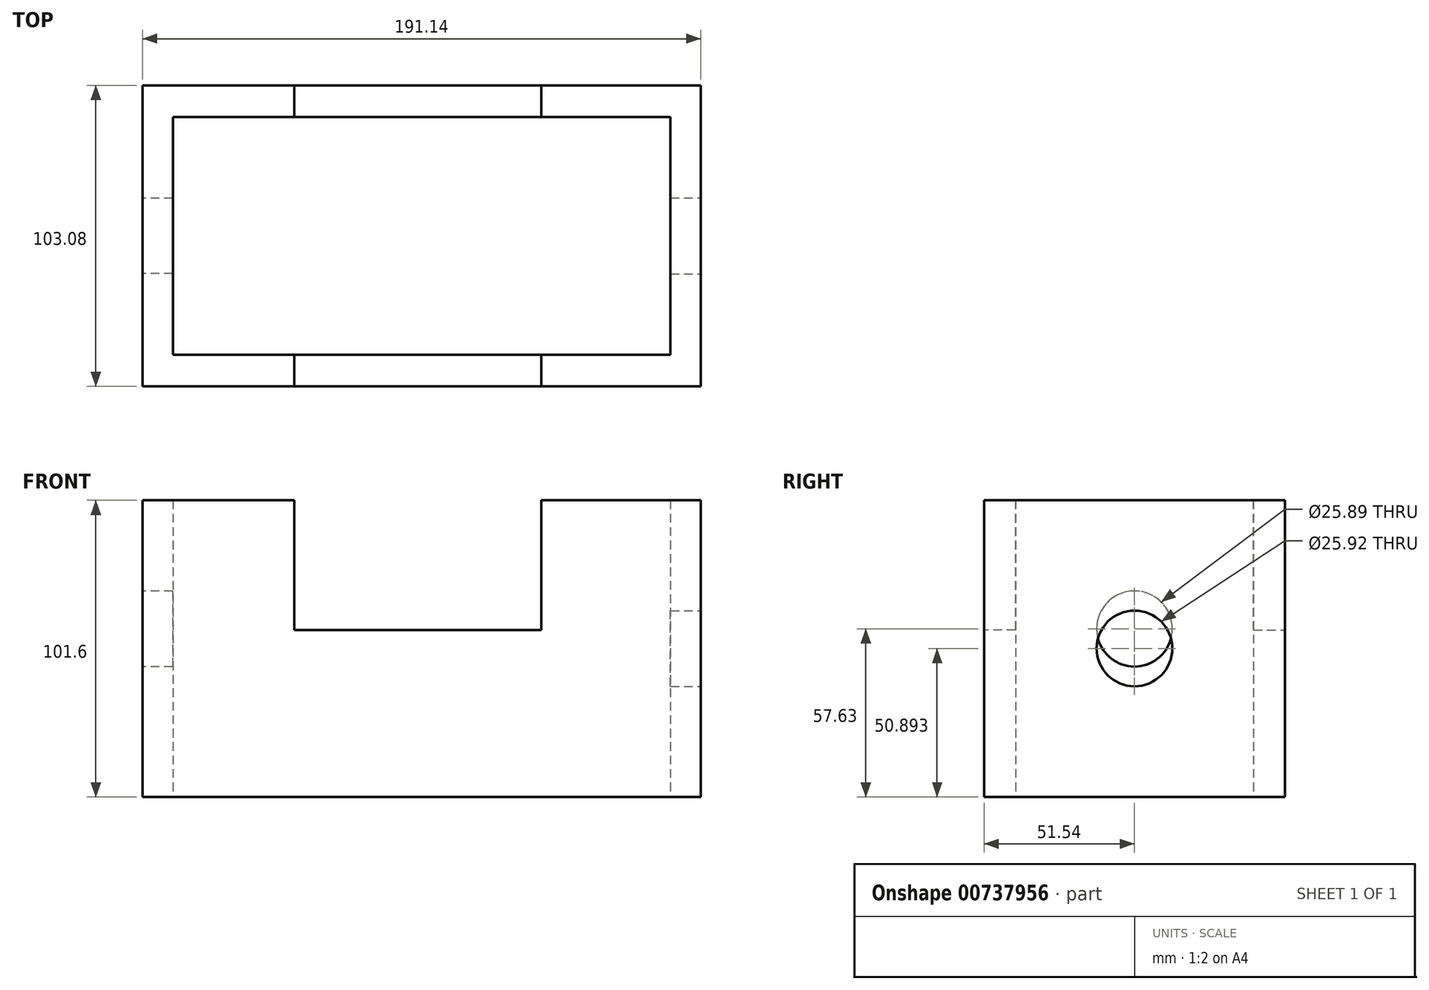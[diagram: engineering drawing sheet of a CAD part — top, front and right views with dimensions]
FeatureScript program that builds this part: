
annotation { "Feature Type Name" : "Feature", "Feature Type Description" : "" }
export const myFeature = defineFeature(function(context is Context, id is Id, definition is map)
    precondition{}
    {
        {
            var Q0;
            Q0=qCreatedBy(makeId("Top.planeOp"),FACE);
            var sketch = newSketch(context, id + "F0", { "sketchPlane" : qUnion([Q0])});
            skLineSegment(sketch, "E0.bottom", {"start": v(95.57, 51.54) * mm, "end": v(-95.57, 51.54) * mm});
            skLineSegment(sketch, "E0.top", {"start": v(95.57, -51.54) * mm, "end": v(-95.57, -51.54) * mm});
            skLineSegment(sketch, "E0.left", {"start": v(95.57, 51.54) * mm, "end": v(95.57, -51.54) * mm});
            skLineSegment(sketch, "E0.right", {"start": v(-95.57, 51.54) * mm, "end": v(-95.57, -51.54) * mm});
            skPoint(sketch, "E0.middle", {"position": v(0, 0) * mm});
            skLineSegment(sketch, "E1.bottom", {"start": v(85.2, 40.75) * mm, "end": v(-85.2, 40.75) * mm});
            skLineSegment(sketch, "E1.top", {"start": v(85.2, -40.75) * mm, "end": v(-85.2, -40.75) * mm});
            skLineSegment(sketch, "E1.left", {"start": v(85.2, 40.75) * mm, "end": v(85.2, -40.75) * mm});
            skLineSegment(sketch, "E1.right", {"start": v(-85.2, 40.75) * mm, "end": v(-85.2, -40.75) * mm});
            skSolve(sketch);
        }
        {
            var Q0;
            Q0=makeQuery(id+"F0.imprint","IMPRINT",FACE,{"disambiguationData":[TD([[makeQuery(id+"F0.imprint","IMPRINT",EDGE,{"derivedFrom":sQuery(id+"F0.wireOp",EDGE,"E0.bottom")}),1.0]])]});
            extrude(context, id + "F1", {"entities" : qUnion([Q0]), "depth" : 101.6 * mm, "offsetDistance" : 25.4 * mm});
        }
        {
            var Q0;
            Q0=makeQuery(id+"F1.opExtrude","CAP_FACE",FACE,{"disambiguationData":[OSD([sQuery(id+"F0.wireOp",EDGE,"E0.bottom"),sQuery(id+"F0.wireOp",EDGE,"E0.top"),sQuery(id+"F0.wireOp",EDGE,"E0.left"),sQuery(id+"F0.wireOp",EDGE,"E0.right"),sQuery(id+"F0.wireOp",EDGE,"E1.bottom"),sQuery(id+"F0.wireOp",EDGE,"E1.top"),sQuery(id+"F0.wireOp",EDGE,"E1.left"),sQuery(id+"F0.wireOp",EDGE,"E1.right")])],"isStart":false});
            var sketch = newSketch(context, id + "F2", { "sketchPlane" : qUnion([Q0])});
            skLineSegment(sketch, "E2", {"start": v(-43.64, -40.75) * mm, "end": v(-43.64, -51.54) * mm});
            skLineSegment(sketch, "E3", {"start": v(40.92, -40.75) * mm, "end": v(40.92, -51.54) * mm});
            skLineSegment(sketch, "E4", {"start": v(49.47, 40.75) * mm, "end": v(49.47, 51.54) * mm});
            skLineSegment(sketch, "E5", {"start": v(-45.47, 40.75) * mm, "end": v(-45.47, 51.54) * mm});
            skSolve(sketch);
        }
        {
            var Q0;
            {var subQ0=sQuery(id+"F2.wireOp",EDGE,"E2");Q0=makeQuery(id+"F2.imprint","IMPRINT",FACE,{"disambiguationData":[TD([[makeQuery(id+"F2.imprint","IMPRINT",EDGE,{"derivedFrom":subQ0}),1.0]])]});}
            extrude(context, id + "F3", {"entities" : qUnion([Q0]), "operationType" : NewBodyOperationType.REMOVE, "oppositeDirection" : true, "depth" : 44.45 * mm, "offsetDistance" : 25.4 * mm});
        }
        {
            var Q0;
            Q0=makeQuery(id+"F1.opExtrude","CAP_FACE",FACE,{"disambiguationData":[OSD([sQuery(id+"F0.wireOp",EDGE,"E0.bottom"),sQuery(id+"F0.wireOp",EDGE,"E0.top"),sQuery(id+"F0.wireOp",EDGE,"E0.left"),sQuery(id+"F0.wireOp",EDGE,"E0.right"),sQuery(id+"F0.wireOp",EDGE,"E1.bottom"),sQuery(id+"F0.wireOp",EDGE,"E1.top"),sQuery(id+"F0.wireOp",EDGE,"E1.left"),sQuery(id+"F0.wireOp",EDGE,"E1.right")])],"isStart":false});
            var sketch = newSketch(context, id + "F4", { "sketchPlane" : qUnion([Q0])});
            skLineSegment(sketch, "E6", {"start": v(-43.64, 40.75) * mm, "end": v(-43.64, 51.54) * mm});
            skLineSegment(sketch, "E7", {"start": v(40.92, 40.75) * mm, "end": v(40.92, 51.54) * mm});
            skSolve(sketch);
        }
        {
            var Q0;
            {var subQ0=sQuery(id+"F4.wireOp",EDGE,"E6");Q0=makeQuery(id+"F4.imprint","IMPRINT",FACE,{"disambiguationData":[TD([[makeQuery(id+"F4.imprint","IMPRINT",EDGE,{"derivedFrom":subQ0}),-1.0]])]});}
            extrude(context, id + "F5", {"entities" : qUnion([Q0]), "operationType" : NewBodyOperationType.REMOVE, "oppositeDirection" : true, "depth" : 44.45 * mm, "offsetDistance" : 25.4 * mm});
        }
        {
            var Q0;
            Q0=makeQuery(id+"F1.opExtrude","SWEPT_FACE",FACE,{"disambiguationData":[OSD([sQuery(id+"F0.wireOp",EDGE,"E0.right")])]});
            var sketch = newSketch(context, id + "F6", { "sketchPlane" : qUnion([Q0])});
            skCircle(sketch, "E8", {"center": v(0, 57.63) * mm, "radius": 12.95 * mm});
            skSolve(sketch);
        }
        {
            var Q0;
            Q0 = qSketchRegion(id + "F6", true);
            extrude(context, id + "F7", {"entities" : qUnion([Q0]), "operationType" : NewBodyOperationType.REMOVE, "oppositeDirection" : true, "depth" : 25.4 * mm, "offsetDistance" : 25.4 * mm});
        }
        {
            var Q0;
            Q0=makeQuery(id+"F1.opExtrude","SWEPT_FACE",FACE,{"disambiguationData":[OSD([sQuery(id+"F0.wireOp",EDGE,"E0.left")])]});
            var sketch = newSketch(context, id + "F8", { "sketchPlane" : qUnion([Q0])});
            skCircle(sketch, "E9", {"center": v(0, 50.9) * mm, "radius": 12.96 * mm});
            skSolve(sketch);
        }
        {
            var Q0;
            Q0 = qSketchRegion(id + "F8", true);
            extrude(context, id + "F9", {"entities" : qUnion([Q0]), "operationType" : NewBodyOperationType.REMOVE, "oppositeDirection" : true, "depth" : 25.4 * mm, "offsetDistance" : 25.4 * mm});
        }
    });
